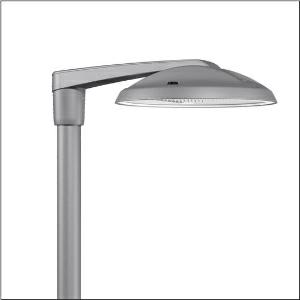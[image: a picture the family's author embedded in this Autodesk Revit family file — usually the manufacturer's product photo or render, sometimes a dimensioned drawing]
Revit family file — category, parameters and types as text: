
# Revit family: dl_r__50_mini___st1_0a_5xa248d33s08me_5901
name_source: partatom
category: Lighting Fixtures
units: mm (PartAtom-declared; Revit-internal decimal feet)

## family parameters
Cut with Voids When Loaded = No
Host = Face
Light Source = No
Part Type = Normal
Room Calculation Point = No
Round Connector Dimension = Use Diameter
Shared = No

## types (1)
- --- (1 x LED, 15380 lm, 110.3 W, 3000K)
    Apparent Load = 110 VA
    CIE Flux Codes = 37 72 97 100 100
    Color Rendering = 70
    Color Temperature = 3000K
    Default Elevation = 1800 mm
    Description = DL® 50 mini, mast luminaire, primary light control with lens, of PMMA, primary optical cover: cover, of toughened safety glass, transparent, light distribution: ST1.0a, light emission: direct distribution, primary light characteristic: asymmetric, installation type: post-top, side-entry, LED, High Power LED, rated luminous flux: 15.380lm, luminous efficacy: 139lm/W, light colour: 730, colour temperature: 3000K, control: overheat protection, constant luminous flux control, time-dependent luminous flux control, flexible luminous flux parameterisation, mains connection: 230..240V, AC, 50/60Hz, connection cable pre-assembled, cable length: 10,5m, start of lifetime: 110W, end of service life: 116W, reduction: 49W, luminaire housing, of diecast aluminium, powder-coated, Siteco® metallic grey (DB 702S), inclination adjustable: 0°, 5°, 10° (post-top) | 0°, -5°, -10°, -15° (side-entry), please order mast post-top element or mast side-entry element separately, diameter: 500mm, height: 115mm, post-top: for spigot size d x l = 76 x 100mm; with reducer (optional accessory) 60 x 100mm | side-entry: for spigot size d x l = 60 x 100mm; with reducer (optional accessory) 42 x 100mm, Smart Interface above, protection rating (complete): IP66, insulation class (complete): insulation class II (safety insulation), certification: CE, ENEC, VDE, impact resistance: IK08, permissible operating ambient temperature for outdoor applications: -25..+40°C, standard-compliant lighting for roads and squares, packaging unit: 1 piece

Light Distribution: ST1.0a
    Height = 115 mm
    Lamp = 1 x LED
    Lamp Light Flux = 15380 lm
    Lamp Power = 110.3 W
    Lamp count = 1
    Length = 500 mm
    Luminous efficacy = 139 lm/W
    Manufacturer = Siteco
    ModVariant = No
    Model = 5XA248D33S08ME
    Number of Poles = 1
    OnlyDefault = Yes
    Power Factor = 1
    Product Name = DL® 50 mini | ST1.0a
    Product group = mast luminaire | pylon top
    ProductGroupID = 6100
    Protection Class = Protection class II
    Protection Degree = IP 66
    RLX_Detail_Level = 1
    RLX_Emergency_Light_Flux = 0 lm
    RLX_Emergency_Type = 0
    RLX_Emergency_Type_DB = No
    RlxData = <blob elided: 106049 chars, md5=4ba00c5a>
    Socket = socket
    Standby Power = 0 W
    System Light Flux = 15380 lm
    System Power = 110 W
    Type Comments = factory setting: luminous flux: 100 % | dim-lin: 254 | 565 mA
    Type Image = l_1251788.jpg
    URL = http://relux.com
    VarID = @adj_023621
    Voltage = 0 V
    Weight = 0.00 kg
    Width = 0 mm  [stored 0 ft]

note: [stored X ft] marks values corroborated as IEEE doubles in the binary element streams (Revit-internal decimal feet)

## geometry (parser evidence)
native form markers: Blend x4, Sweep x10
no freeform markers — native parametric forms only
